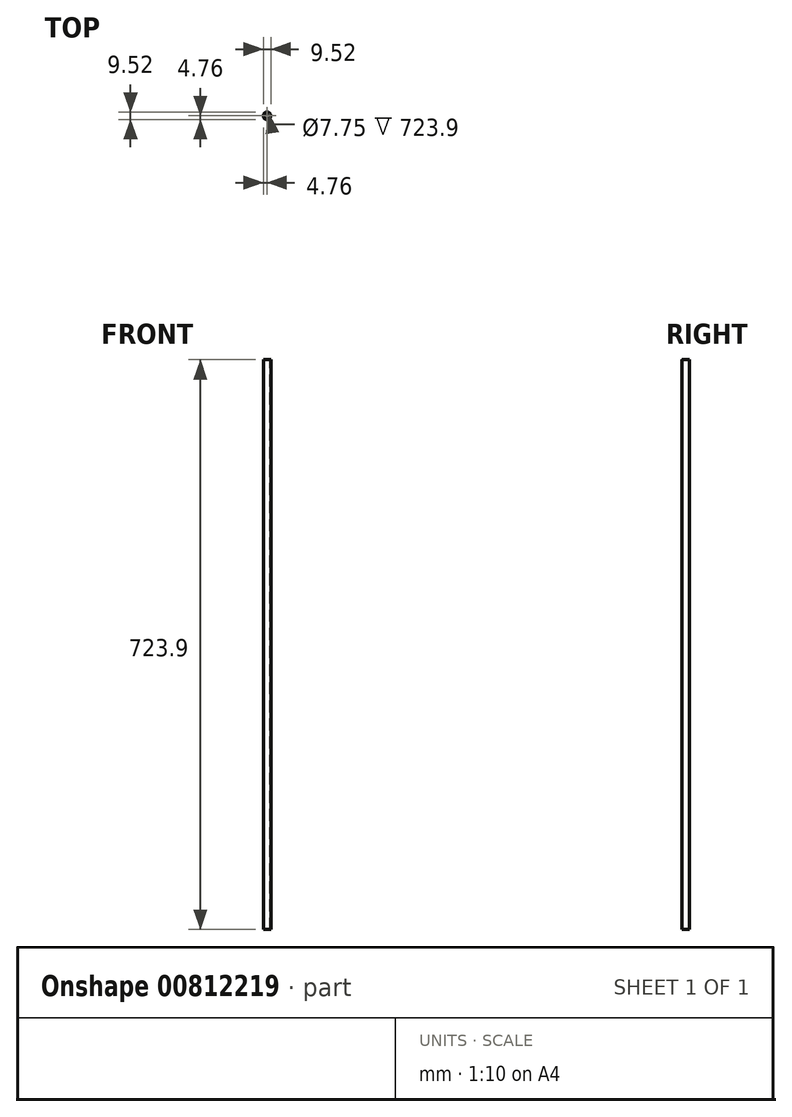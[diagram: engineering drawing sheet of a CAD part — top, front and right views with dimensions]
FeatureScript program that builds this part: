
annotation { "Feature Type Name" : "Feature", "Feature Type Description" : "" }
export const myFeature = defineFeature(function(context is Context, id is Id, definition is map)
    precondition{}
    {
        {
            var Q0;
            Q0=qCreatedBy(makeId("Front.planeOp"),FACE);
            var sketch = newSketch(context, id + "F0", { "sketchPlane" : qUnion([Q0])});
            skLineSegment(sketch, "E0", {"start": v(0, 0) * mm, "end": v(-127, -266.7) * mm});
            skLineSegment(sketch, "E1", {"start": v(0, 0) * mm, "end": v(127, -266.7) * mm});
            skLineSegment(sketch, "E2", {"start": v(-127, -266.7) * mm, "end": v(127, -266.7) * mm});
            skLineSegment(sketch, "E3", {"start": v(-127, -266.7) * mm, "end": v(-127, -723.9) * mm});
            skLineSegment(sketch, "E4", {"start": v(127, -266.7) * mm, "end": v(127, -723.9) * mm});
            skLineSegment(sketch, "E5", {"start": v(127, -266.7) * mm, "end": v(-127, -723.9) * mm});
            skSolve(sketch);
        }
        {
            var Q0;
            Q0=qCreatedBy(makeId("Top.planeOp"),FACE);
            var sketch = newSketch(context, id + "F1", { "sketchPlane" : qUnion([Q0])});
            skCircle(sketch, "E6", {"center": v(127, 0) * mm, "radius": 4.76 * mm});
            skCircle(sketch, "E7", {"center": v(127, 0) * mm, "radius": 3.87 * mm});
            skSolve(sketch);
        }
        {
            var Q0;
            Q0 = qSketchRegion(id + "F1", true);
            extrude(context, id + "F2", {"entities" : qUnion([Q0]), "depth" : -723.9 * mm, "offsetDistance" : 25.4 * mm});
        }
    });
